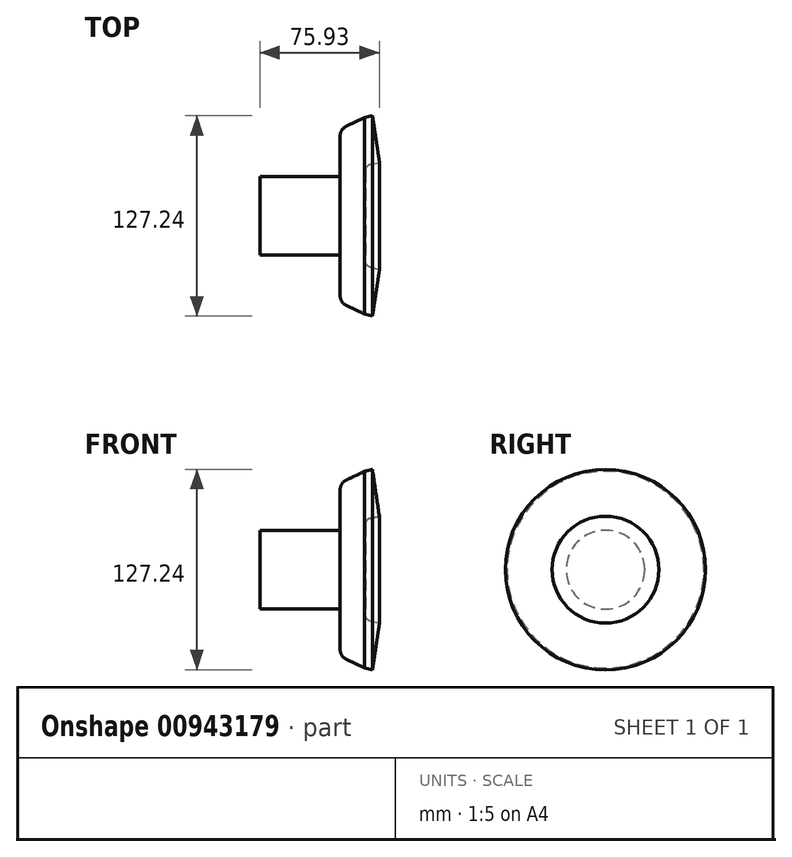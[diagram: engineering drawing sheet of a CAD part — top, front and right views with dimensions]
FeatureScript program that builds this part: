
annotation { "Feature Type Name" : "Feature", "Feature Type Description" : "" }
export const myFeature = defineFeature(function(context is Context, id is Id, definition is map)
    precondition{}
    {
        {
            var Q0;
            Q0=qCreatedBy(makeId("Front.planeOp"),FACE);
            var sketch = newSketch(context, id + "F0", { "sketchPlane" : qUnion([Q0])});
            skLineSegment(sketch, "E0", {"start": v(20, 25) * mm, "end": v(20, 50.6) * mm});
            skLineSegment(sketch, "E1", {"start": v(35.63, 62.5) * mm, "end": v(23.97, 56.9) * mm});
            skLineSegment(sketch, "E2", {"start": v(20, 50.6) * mm, "end": v(20, 26) * mm});
            skPoint(sketch, "E3.endSnap0", {"position": v(20, 0) * mm});
            skLineSegment(sketch, "E4", {"start": v(35.63, 62.5) * mm, "end": v(40.5, 63.62) * mm});
            skLineSegment(sketch, "E5", {"start": v(40.5, 63.62) * mm, "end": v(44.93, 33.95) * mm});
            skPoint(sketch, "E6.endSnap0", {"position": v(42.82, 31.25) * mm});
            skPoint(sketch, "E7.newPointA", {"position": v(20, 25) * mm});
            skArc(sketch, "E7.filletArc", {"start": v(19, 25) * mm, "mid": v(19.7, 25.3) * mm, "end": v(20, 26) * mm});
            skLineSegment(sketch, "E8", {"start": v(35.63, 62.5) * mm, "end": v(30.37, 59.98) * mm});
            skLineSegment(sketch, "E9", {"start": v(36, 0) * mm, "end": v(36, 28.71) * mm});
            skLineSegment(sketch, "E10", {"start": v(39.1, 32.6) * mm, "end": v(44.93, 33.95) * mm});
            skPoint(sketch, "E11.visualSharp", {"position": v(36, 31.9) * mm});
            skArc(sketch, "E11.filletArc", {"start": v(39.1, 32.6) * mm, "mid": v(36.87, 31.2) * mm, "end": v(36, 28.71) * mm});
            skLineSegment(sketch, "E12", {"start": v(19, 25) * mm, "end": v(-31, 25) * mm});
            skLineSegment(sketch, "E13", {"start": v(-31, 25) * mm, "end": v(-31, 0) * mm});
            skLineSegment(sketch, "E14", {"start": v(-31, 0) * mm, "end": v(36, 0) * mm});
            skPoint(sketch, "E15.visualSharp", {"position": v(20, 55) * mm});
            skArc(sketch, "E15.filletArc", {"start": v(23.97, 56.9) * mm, "mid": v(21.08, 54.32) * mm, "end": v(20, 50.6) * mm});
            skSolve(sketch);
        }
        {
            var Q0;
            Q0 = qSketchRegion(id + "F0", true);
            var Q1;
            Q1=sQuery(id+"F0.wireOp",EDGE,"E14");
            revolve(context, id + "F1", {"surfaceOperationType" : NewSurfaceOperationType.NEW, "entities" : qUnion([Q0]), "axis" : qUnion([Q1]), "revolveType" : RevolveType.FULL});
        }
    });
